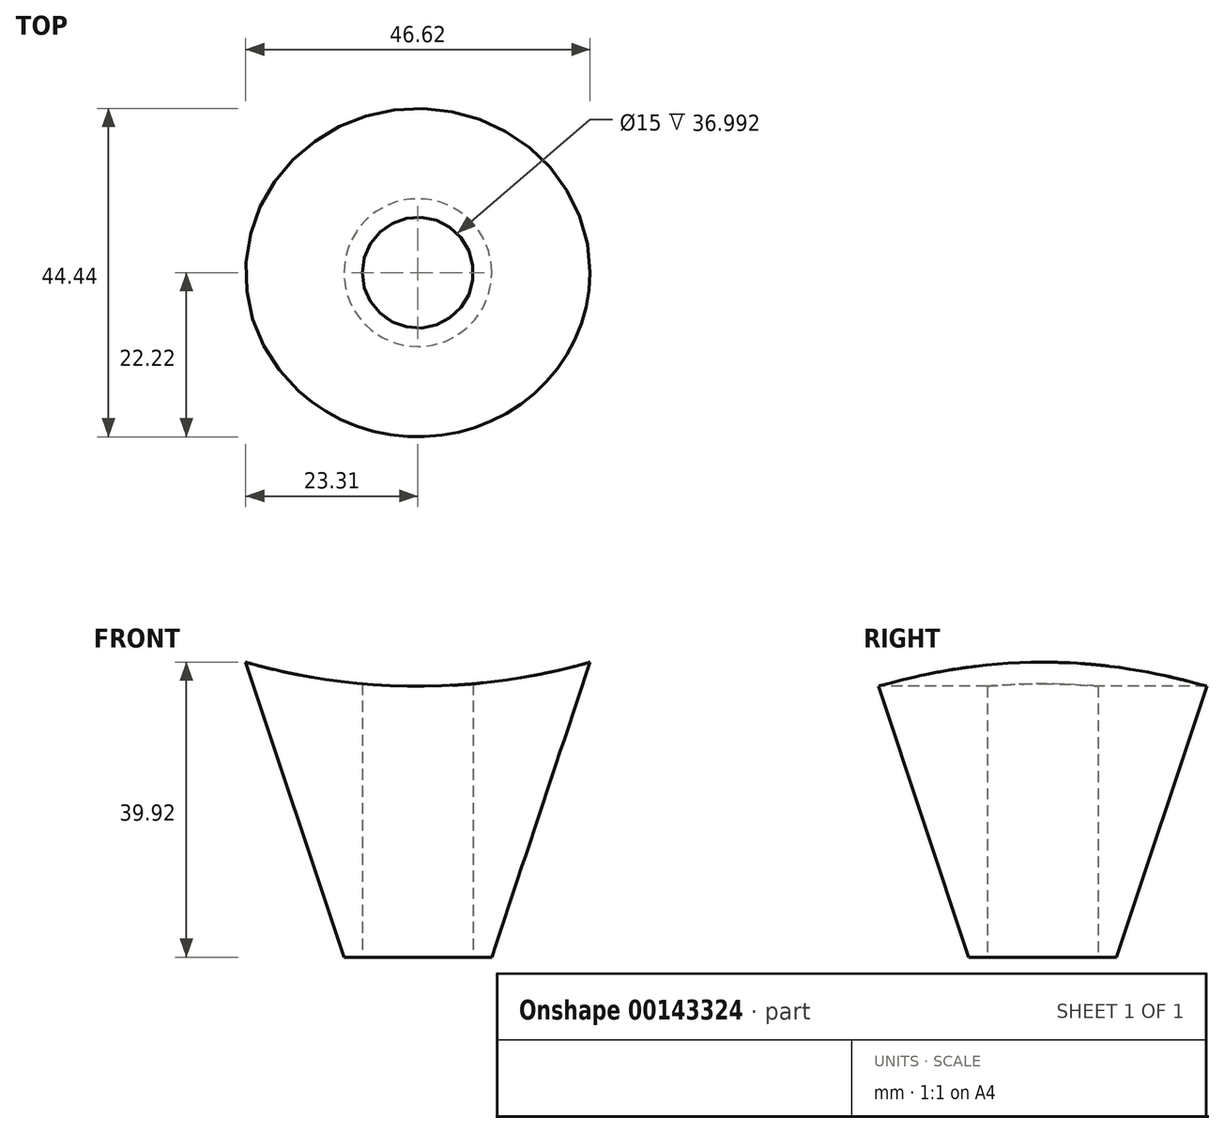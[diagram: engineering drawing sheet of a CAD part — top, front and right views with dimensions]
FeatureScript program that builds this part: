
annotation { "Feature Type Name" : "Feature", "Feature Type Description" : "" }
export const myFeature = defineFeature(function(context is Context, id is Id, definition is map)
    precondition{}
    {
        {
            var Q0;
            Q0=qCreatedBy(makeId("Front.planeOp"),FACE);
            var sketch = newSketch(context, id + "F0", { "sketchPlane" : qUnion([Q0])});
            skLineSegment(sketch, "E0", {"start": v(-10, 0) * mm, "end": v(10, 0) * mm});
            skLineSegment(sketch, "E1", {"start": v(-20, 30) * mm, "end": v(-10, 0) * mm});
            skLineSegment(sketch, "E2", {"start": v(10, 0) * mm, "end": v(20, 30) * mm});
            skPoint(sketch, "E3.endSnap0", {"position": v(0, 15) * mm});
            skLineSegment(sketch, "E4", {"start": v(-10, 0) * mm, "end": v(-23.33, 40) * mm});
            skLineSegment(sketch, "E5", {"start": v(-23.33, 40) * mm, "end": v(0, 40) * mm});
            skLineSegment(sketch, "E6", {"start": v(10, 0) * mm, "end": v(23.33, 40) * mm});
            skLineSegment(sketch, "E7", {"start": v(23.33, 40) * mm, "end": v(0, 40) * mm});
            skLineSegment(sketch, "E8", {"start": v(-23.33, 40) * mm, "end": v(23.33, 40) * mm});
            skLineSegment(sketch, "E9", {"start": v(0, 40) * mm, "end": v(0, 0) * mm});
            skSolve(sketch);
        }
        {
            var Q0;
            {var subQ3=sQuery(id+"F0.wireOp",EDGE,"E9");Q0=makeQuery(id+"F0.imprint","IMPRINT",FACE,{"disambiguationData":[TD([[makeQuery(id+"F0.imprint","IMPRINT",EDGE,{"derivedFrom":subQ3}),-1.0]])]});}
            var Q1;
            Q1=sQuery(id+"F0.wireOp",EDGE,"E9");
            revolve(context, id + "F1", {"entities" : qUnion([Q0]), "axis" : qUnion([Q1]), "revolveType" : RevolveType.FULL});
        }
        {
            var Q0;
            Q0=qCreatedBy(makeId("Top.planeOp"),FACE);
            var sketch = newSketch(context, id + "F2", { "sketchPlane" : qUnion([Q0])});
            skCircle(sketch, "E10", {"center": v(0, 0) * mm, "radius": 7.5 * mm});
            skSolve(sketch);
        }
        {
            var Q0;
            Q0 = qSketchRegion(id + "F2", true);
            extrude(context, id + "F3", {"entities" : qUnion([Q0]), "operationType" : NewBodyOperationType.REMOVE, "depth" : 50 * mm});
        }
        {
            var Q0;
            Q0=qCreatedBy(makeId("Front.planeOp"),FACE);
            var sketch = newSketch(context, id + "F4", { "sketchPlane" : qUnion([Q0])});
            skArc(sketch, "E11.0", {"start": v(-39.27, 46.28) * mm, "mid": v(0, 57.35) * mm, "end": v(39.27, 46.28) * mm});
            skArc(sketch, "E11.1", {"start": v(-39.27, 46.28) * mm, "mid": v(0, 36.66) * mm, "end": v(39.27, 46.28) * mm});
            skSolve(sketch);
        }
        {
            var Q0;
            Q0 = qSketchRegion(id + "F4", true);
            extrude(context, id + "F5", {"entities" : qUnion([Q0]), "operationType" : NewBodyOperationType.REMOVE, "endBound" : BoundingType.SYMMETRIC, "oppositeDirection" : true, "depth" : 50 * mm});
        }
    });
